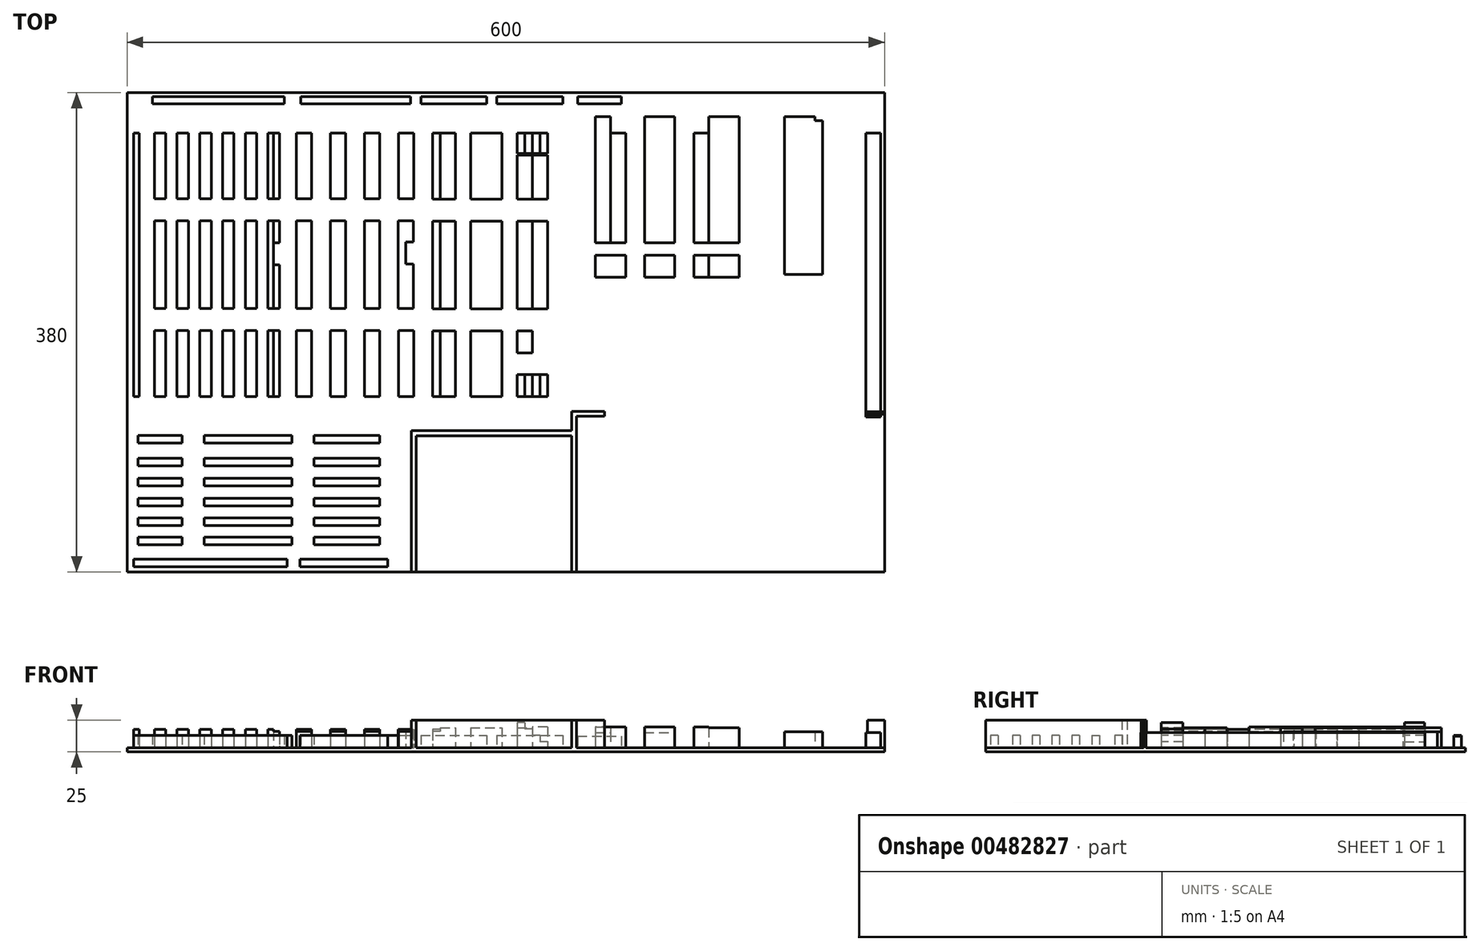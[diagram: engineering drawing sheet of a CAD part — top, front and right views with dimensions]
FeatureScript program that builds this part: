
annotation { "Feature Type Name" : "Feature", "Feature Type Description" : "" }
export const myFeature = defineFeature(function(context is Context, id is Id, definition is map)
    precondition{}
    {
        {
            var Q0;
            Q0=qCreatedBy(makeId("Top.planeOp"),FACE);
            var sketch = newSketch(context, id + "F0", { "sketchPlane" : qUnion([Q0])});
            skLineSegment(sketch, "E0.bottom", {"start": v(300, 190) * mm, "end": v(-300, 190) * mm});
            skLineSegment(sketch, "E0.top", {"start": v(300, -190) * mm, "end": v(-300, -190) * mm});
            skLineSegment(sketch, "E0.left", {"start": v(300, 190) * mm, "end": v(300, -190) * mm});
            skLineSegment(sketch, "E0.right", {"start": v(-300, 190) * mm, "end": v(-300, -190) * mm});
            skPoint(sketch, "E0.middle", {"position": v(0, 0) * mm});
            skLineSegment(sketch, "E1", {"start": v(-75, -78) * mm, "end": v(-75, -190) * mm});
            skLineSegment(sketch, "E2", {"start": v(-75, -78) * mm, "end": v(52, -78) * mm});
            skLineSegment(sketch, "E3", {"start": v(300, -63) * mm, "end": v(286.5, -63) * mm});
            skLineSegment(sketch, "E4", {"start": v(52, -78) * mm, "end": v(52, -62.65) * mm});
            skLineSegment(sketch, "E5", {"start": v(52, -62.65) * mm, "end": v(78, -62.65) * mm});
            skLineSegment(sketch, "E6.0", {"start": v(56, -66.65) * mm, "end": v(78, -66.65) * mm});
            skLineSegment(sketch, "E6.1", {"start": v(56, -78) * mm, "end": v(56, -66.65) * mm});
            skLineSegment(sketch, "E6.2", {"start": v(56, -78) * mm, "end": v(56, -190) * mm});
            skLineSegment(sketch, "E7", {"start": v(78, -62.65) * mm, "end": v(78, -66.65) * mm});
            skLineSegment(sketch, "E8.0", {"start": v(300, -65) * mm, "end": v(286.5, -65) * mm});
            skLineSegment(sketch, "E9", {"start": v(286.5, -63) * mm, "end": v(286.5, -65) * mm});
            skLineSegment(sketch, "E10.0", {"start": v(-71, -82) * mm, "end": v(-71, -190) * mm});
            skLineSegment(sketch, "E10.1", {"start": v(-71, -82) * mm, "end": v(52, -82) * mm});
            skLineSegment(sketch, "E11.0", {"start": v(52, -82) * mm, "end": v(52, -190) * mm});
            skLineSegment(sketch, "E12.0", {"start": v(304, 194) * mm, "end": v(-304, 194) * mm});
            skLineSegment(sketch, "E12.1", {"start": v(304, 194) * mm, "end": v(304, -194) * mm});
            skLineSegment(sketch, "E12.2", {"start": v(304, -194) * mm, "end": v(-304, -194) * mm});
            skLineSegment(sketch, "E12.3", {"start": v(-304, 194) * mm, "end": v(-304, -194) * mm});
            skLineSegment(sketch, "E13.bottom", {"start": v(-280, 187) * mm, "end": v(-175.6, 187) * mm});
            skLineSegment(sketch, "E13.top", {"start": v(-280, 181) * mm, "end": v(-175.6, 181) * mm});
            skLineSegment(sketch, "E13.left", {"start": v(-280, 187) * mm, "end": v(-280, 181) * mm});
            skLineSegment(sketch, "E13.right", {"start": v(-175.6, 187) * mm, "end": v(-175.6, 181) * mm});
            skLineSegment(sketch, "E14.bottom", {"start": v(-162.42, 187) * mm, "end": v(-75.42, 187) * mm});
            skLineSegment(sketch, "E14.top", {"start": v(-162.42, 181) * mm, "end": v(-75.42, 181) * mm});
            skLineSegment(sketch, "E14.left", {"start": v(-162.42, 187) * mm, "end": v(-162.42, 181) * mm});
            skLineSegment(sketch, "E14.right", {"start": v(-75.42, 187) * mm, "end": v(-75.42, 181) * mm});
            skLineSegment(sketch, "E15.bottom", {"start": v(-67.42, 187) * mm, "end": v(-15.22, 187) * mm});
            skLineSegment(sketch, "E15.top", {"start": v(-67.42, 181) * mm, "end": v(-15.22, 181) * mm});
            skLineSegment(sketch, "E15.left", {"start": v(-67.42, 187) * mm, "end": v(-67.42, 181) * mm});
            skLineSegment(sketch, "E15.right", {"start": v(-15.22, 187) * mm, "end": v(-15.22, 181) * mm});
            skLineSegment(sketch, "E16.bottom", {"start": v(56.8, 187) * mm, "end": v(91.6, 187) * mm});
            skLineSegment(sketch, "E16.top", {"start": v(56.8, 181) * mm, "end": v(91.6, 181) * mm});
            skLineSegment(sketch, "E16.left", {"start": v(56.8, 187) * mm, "end": v(56.8, 181) * mm});
            skLineSegment(sketch, "E16.right", {"start": v(91.6, 187) * mm, "end": v(91.6, 181) * mm});
            skLineSegment(sketch, "E17.bottom", {"start": v(-295, 158) * mm, "end": v(-290.5, 158) * mm});
            skLineSegment(sketch, "E17.top", {"start": v(-295, 18.8) * mm, "end": v(-290.5, 18.8) * mm});
            skLineSegment(sketch, "E17.left", {"start": v(-295, 158) * mm, "end": v(-295, 18.8) * mm});
            skLineSegment(sketch, "E17.right", {"start": v(-290.5, 158) * mm, "end": v(-290.5, 18.8) * mm});
            skLineSegment(sketch, "E18.top", {"start": v(-295, -50.8) * mm, "end": v(-290.5, -50.8) * mm});
            skLineSegment(sketch, "E18.left", {"start": v(-295, 18.8) * mm, "end": v(-295, -50.8) * mm});
            skLineSegment(sketch, "E18.right", {"start": v(-290.5, 18.8) * mm, "end": v(-290.5, -50.8) * mm});
            skLineSegment(sketch, "E19.bottom", {"start": v(-278.5, 158) * mm, "end": v(-269.5, 158) * mm});
            skLineSegment(sketch, "E19.top", {"start": v(-278.5, 105.8) * mm, "end": v(-269.5, 105.8) * mm});
            skLineSegment(sketch, "E19.left", {"start": v(-278.5, 158) * mm, "end": v(-278.5, 105.8) * mm});
            skLineSegment(sketch, "E19.right", {"start": v(-269.5, 158) * mm, "end": v(-269.5, 105.8) * mm});
            skLineSegment(sketch, "E20.1.0.0", {"start": v(-260.5, 158) * mm, "end": v(-251.5, 158) * mm});
            skLineSegment(sketch, "E20.1.0.1", {"start": v(-260.5, 158) * mm, "end": v(-260.5, 105.8) * mm});
            skLineSegment(sketch, "E20.1.0.2", {"start": v(-251.5, 158) * mm, "end": v(-251.5, 105.8) * mm});
            skLineSegment(sketch, "E20.1.0.3", {"start": v(-260.5, 105.8) * mm, "end": v(-251.5, 105.8) * mm});
            skLineSegment(sketch, "E20.2.0.0", {"start": v(-242.5, 158) * mm, "end": v(-233.5, 158) * mm});
            skLineSegment(sketch, "E20.2.0.1", {"start": v(-242.5, 158) * mm, "end": v(-242.5, 105.8) * mm});
            skLineSegment(sketch, "E20.2.0.2", {"start": v(-233.5, 158) * mm, "end": v(-233.5, 105.8) * mm});
            skLineSegment(sketch, "E20.2.0.3", {"start": v(-242.5, 105.8) * mm, "end": v(-233.5, 105.8) * mm});
            skLineSegment(sketch, "E20.3.0.0", {"start": v(-224.5, 158) * mm, "end": v(-215.5, 158) * mm});
            skLineSegment(sketch, "E20.3.0.1", {"start": v(-224.5, 158) * mm, "end": v(-224.5, 105.8) * mm});
            skLineSegment(sketch, "E20.3.0.2", {"start": v(-215.5, 158) * mm, "end": v(-215.5, 105.8) * mm});
            skLineSegment(sketch, "E20.3.0.3", {"start": v(-224.5, 105.8) * mm, "end": v(-215.5, 105.8) * mm});
            skLineSegment(sketch, "E20.4.0.0", {"start": v(-206.5, 158) * mm, "end": v(-197.5, 158) * mm});
            skLineSegment(sketch, "E20.4.0.1", {"start": v(-206.5, 158) * mm, "end": v(-206.5, 105.8) * mm});
            skLineSegment(sketch, "E20.4.0.2", {"start": v(-197.5, 158) * mm, "end": v(-197.5, 105.8) * mm});
            skLineSegment(sketch, "E20.4.0.3", {"start": v(-206.5, 105.8) * mm, "end": v(-197.5, 105.8) * mm});
            skLineSegment(sketch, "E21.bottom", {"start": v(-278.5, 88.4) * mm, "end": v(-269.5, 88.4) * mm});
            skLineSegment(sketch, "E21.top", {"start": v(-278.5, 18.8) * mm, "end": v(-269.5, 18.8) * mm});
            skLineSegment(sketch, "E21.left", {"start": v(-278.5, 88.4) * mm, "end": v(-278.5, 18.8) * mm});
            skLineSegment(sketch, "E21.right", {"start": v(-269.5, 88.4) * mm, "end": v(-269.5, 18.8) * mm});
            skLineSegment(sketch, "E22.1.0.0", {"start": v(-260.5, 88.4) * mm, "end": v(-251.5, 88.4) * mm});
            skLineSegment(sketch, "E22.1.0.1", {"start": v(-251.5, 88.4) * mm, "end": v(-251.5, 18.8) * mm});
            skLineSegment(sketch, "E22.1.0.2", {"start": v(-260.5, 88.4) * mm, "end": v(-260.5, 18.8) * mm});
            skLineSegment(sketch, "E22.1.0.3", {"start": v(-260.5, 18.8) * mm, "end": v(-251.5, 18.8) * mm});
            skLineSegment(sketch, "E22.2.0.0", {"start": v(-242.5, 88.4) * mm, "end": v(-233.5, 88.4) * mm});
            skLineSegment(sketch, "E22.2.0.1", {"start": v(-233.5, 88.4) * mm, "end": v(-233.5, 18.8) * mm});
            skLineSegment(sketch, "E22.2.0.2", {"start": v(-242.5, 88.4) * mm, "end": v(-242.5, 18.8) * mm});
            skLineSegment(sketch, "E22.2.0.3", {"start": v(-242.5, 18.8) * mm, "end": v(-233.5, 18.8) * mm});
            skLineSegment(sketch, "E22.3.0.0", {"start": v(-224.5, 88.4) * mm, "end": v(-215.5, 88.4) * mm});
            skLineSegment(sketch, "E22.3.0.1", {"start": v(-215.5, 88.4) * mm, "end": v(-215.5, 18.8) * mm});
            skLineSegment(sketch, "E22.3.0.2", {"start": v(-224.5, 88.4) * mm, "end": v(-224.5, 18.8) * mm});
            skLineSegment(sketch, "E22.3.0.3", {"start": v(-224.5, 18.8) * mm, "end": v(-215.5, 18.8) * mm});
            skLineSegment(sketch, "E22.4.0.0", {"start": v(-206.5, 88.4) * mm, "end": v(-197.5, 88.4) * mm});
            skLineSegment(sketch, "E22.4.0.1", {"start": v(-197.5, 88.4) * mm, "end": v(-197.5, 18.8) * mm});
            skLineSegment(sketch, "E22.4.0.2", {"start": v(-206.5, 88.4) * mm, "end": v(-206.5, 18.8) * mm});
            skLineSegment(sketch, "E22.4.0.3", {"start": v(-206.5, 18.8) * mm, "end": v(-197.5, 18.8) * mm});
            skLineSegment(sketch, "E23.bottom", {"start": v(-278.5, 1.4) * mm, "end": v(-269.5, 1.4) * mm});
            skLineSegment(sketch, "E23.top", {"start": v(-278.5, -50.8) * mm, "end": v(-269.5, -50.8) * mm});
            skLineSegment(sketch, "E23.left", {"start": v(-278.5, 1.4) * mm, "end": v(-278.5, -50.8) * mm});
            skLineSegment(sketch, "E23.right", {"start": v(-269.5, 1.4) * mm, "end": v(-269.5, -50.8) * mm});
            skLineSegment(sketch, "E24.1.0.0", {"start": v(-260.5, 1.4) * mm, "end": v(-260.5, -50.8) * mm});
            skLineSegment(sketch, "E24.1.0.1", {"start": v(-260.5, 1.4) * mm, "end": v(-251.5, 1.4) * mm});
            skLineSegment(sketch, "E24.1.0.2", {"start": v(-251.5, 1.4) * mm, "end": v(-251.5, -50.8) * mm});
            skLineSegment(sketch, "E24.1.0.3", {"start": v(-260.5, -50.8) * mm, "end": v(-251.5, -50.8) * mm});
            skLineSegment(sketch, "E24.2.0.0", {"start": v(-242.5, 1.4) * mm, "end": v(-242.5, -50.8) * mm});
            skLineSegment(sketch, "E24.2.0.1", {"start": v(-242.5, 1.4) * mm, "end": v(-233.5, 1.4) * mm});
            skLineSegment(sketch, "E24.2.0.2", {"start": v(-233.5, 1.4) * mm, "end": v(-233.5, -50.8) * mm});
            skLineSegment(sketch, "E24.2.0.3", {"start": v(-242.5, -50.8) * mm, "end": v(-233.5, -50.8) * mm});
            skLineSegment(sketch, "E24.3.0.0", {"start": v(-224.5, 1.4) * mm, "end": v(-224.5, -50.8) * mm});
            skLineSegment(sketch, "E24.3.0.1", {"start": v(-224.5, 1.4) * mm, "end": v(-215.5, 1.4) * mm});
            skLineSegment(sketch, "E24.3.0.2", {"start": v(-215.5, 1.4) * mm, "end": v(-215.5, -50.8) * mm});
            skLineSegment(sketch, "E24.3.0.3", {"start": v(-224.5, -50.8) * mm, "end": v(-215.5, -50.8) * mm});
            skLineSegment(sketch, "E24.4.0.0", {"start": v(-206.5, 1.4) * mm, "end": v(-206.5, -50.8) * mm});
            skLineSegment(sketch, "E24.4.0.1", {"start": v(-206.5, 1.4) * mm, "end": v(-197.5, 1.4) * mm});
            skLineSegment(sketch, "E24.4.0.2", {"start": v(-197.5, 1.4) * mm, "end": v(-197.5, -50.8) * mm});
            skLineSegment(sketch, "E24.4.0.3", {"start": v(-206.5, -50.8) * mm, "end": v(-197.5, -50.8) * mm});
            skLineSegment(sketch, "E25.bottom", {"start": v(-188.5, 1.4) * mm, "end": v(-184, 1.4) * mm});
            skLineSegment(sketch, "E25.top", {"start": v(-188.5, -50.8) * mm, "end": v(-184, -50.8) * mm});
            skLineSegment(sketch, "E25.left", {"start": v(-188.5, 1.4) * mm, "end": v(-188.5, -50.8) * mm});
            skLineSegment(sketch, "E25.right", {"start": v(-184, 1.4) * mm, "end": v(-184, -50.8) * mm});
            skLineSegment(sketch, "E26.bottom", {"start": v(-188.5, 158) * mm, "end": v(-184, 158) * mm});
            skLineSegment(sketch, "E26.top", {"start": v(-188.5, 105.8) * mm, "end": v(-184, 105.8) * mm});
            skLineSegment(sketch, "E26.left", {"start": v(-188.5, 158) * mm, "end": v(-188.5, 105.8) * mm});
            skLineSegment(sketch, "E26.right", {"start": v(-184, 158) * mm, "end": v(-184, 105.8) * mm});
            skLineSegment(sketch, "E27.bottom", {"start": v(-188.5, 88.4) * mm, "end": v(-184, 88.4) * mm});
            skLineSegment(sketch, "E27.top", {"start": v(-188.5, 18.8) * mm, "end": v(-184, 18.8) * mm});
            skLineSegment(sketch, "E27.left", {"start": v(-188.5, 88.4) * mm, "end": v(-188.5, 18.8) * mm});
            skLineSegment(sketch, "E27.right", {"start": v(-184, 88.4) * mm, "end": v(-184, 18.8) * mm});
            skLineSegment(sketch, "E28", {"start": v(-184, 1.4) * mm, "end": v(-179.5, 1.4) * mm});
            skLineSegment(sketch, "E29", {"start": v(-179.5, 1.4) * mm, "end": v(-179.5, -50.8) * mm});
            skLineSegment(sketch, "E30", {"start": v(-179.5, -50.8) * mm, "end": v(-184, -50.8) * mm});
            skLineSegment(sketch, "E31", {"start": v(-184, 88.4) * mm, "end": v(-179.5, 88.4) * mm});
            skLineSegment(sketch, "E32", {"start": v(-179.5, 18.8) * mm, "end": v(-184, 18.8) * mm});
            skLineSegment(sketch, "E33", {"start": v(-184, 158) * mm, "end": v(-179.5, 158) * mm});
            skLineSegment(sketch, "E34", {"start": v(-179.5, 158) * mm, "end": v(-179.5, 105.8) * mm});
            skLineSegment(sketch, "E35", {"start": v(-179.5, 105.8) * mm, "end": v(-184, 105.8) * mm});
            skLineSegment(sketch, "E36", {"start": v(-179.5, 88.4) * mm, "end": v(-179.5, 71) * mm});
            skLineSegment(sketch, "E37", {"start": v(-179.5, 71) * mm, "end": v(-184, 71) * mm});
            skLineSegment(sketch, "E38", {"start": v(-179.5, 18.8) * mm, "end": v(-179.5, 53.6) * mm});
            skLineSegment(sketch, "E39", {"start": v(-179.5, 53.6) * mm, "end": v(-184, 53.6) * mm});
            skLineSegment(sketch, "E40.bottom", {"start": v(-166, 158) * mm, "end": v(-154, 158) * mm});
            skLineSegment(sketch, "E40.top", {"start": v(-166, 105.8) * mm, "end": v(-154, 105.8) * mm});
            skLineSegment(sketch, "E40.left", {"start": v(-166, 158) * mm, "end": v(-166, 105.8) * mm});
            skLineSegment(sketch, "E40.right", {"start": v(-154, 158) * mm, "end": v(-154, 105.8) * mm});
            skLineSegment(sketch, "E41.bottom", {"start": v(-166, 88.4) * mm, "end": v(-154, 88.4) * mm});
            skLineSegment(sketch, "E41.top", {"start": v(-166, 18.8) * mm, "end": v(-154, 18.8) * mm});
            skLineSegment(sketch, "E41.left", {"start": v(-166, 88.4) * mm, "end": v(-166, 18.8) * mm});
            skLineSegment(sketch, "E41.right", {"start": v(-154, 88.4) * mm, "end": v(-154, 18.8) * mm});
            skLineSegment(sketch, "E42.bottom", {"start": v(-166, 1.4) * mm, "end": v(-154, 1.4) * mm});
            skLineSegment(sketch, "E42.top", {"start": v(-166, -50.8) * mm, "end": v(-154, -50.8) * mm});
            skLineSegment(sketch, "E42.left", {"start": v(-166, 1.4) * mm, "end": v(-166, -50.8) * mm});
            skLineSegment(sketch, "E42.right", {"start": v(-154, 1.4) * mm, "end": v(-154, -50.8) * mm});
            skLineSegment(sketch, "E43.1.0.0", {"start": v(-139, 158) * mm, "end": v(-127, 158) * mm});
            skLineSegment(sketch, "E43.1.0.1", {"start": v(-139, 158) * mm, "end": v(-139, 105.8) * mm});
            skLineSegment(sketch, "E43.1.0.2", {"start": v(-127, 158) * mm, "end": v(-127, 105.8) * mm});
            skLineSegment(sketch, "E43.1.0.3", {"start": v(-139, 105.8) * mm, "end": v(-127, 105.8) * mm});
            skLineSegment(sketch, "E43.1.0.4", {"start": v(-139, 88.4) * mm, "end": v(-127, 88.4) * mm});
            skLineSegment(sketch, "E43.1.0.5", {"start": v(-139, 88.4) * mm, "end": v(-139, 18.8) * mm});
            skLineSegment(sketch, "E43.1.0.6", {"start": v(-127, 88.4) * mm, "end": v(-127, 18.8) * mm});
            skLineSegment(sketch, "E43.1.0.7", {"start": v(-139, 18.8) * mm, "end": v(-127, 18.8) * mm});
            skLineSegment(sketch, "E43.1.0.8", {"start": v(-139, 1.4) * mm, "end": v(-127, 1.4) * mm});
            skLineSegment(sketch, "E43.1.0.9", {"start": v(-127, 1.4) * mm, "end": v(-127, -50.8) * mm});
            skLineSegment(sketch, "E43.1.0.10", {"start": v(-139, 1.4) * mm, "end": v(-139, -50.8) * mm});
            skLineSegment(sketch, "E43.1.0.11", {"start": v(-139, -50.8) * mm, "end": v(-127, -50.8) * mm});
            skLineSegment(sketch, "E43.2.0.0", {"start": v(-112, 158) * mm, "end": v(-100, 158) * mm});
            skLineSegment(sketch, "E43.2.0.1", {"start": v(-112, 158) * mm, "end": v(-112, 105.8) * mm});
            skLineSegment(sketch, "E43.2.0.2", {"start": v(-100, 158) * mm, "end": v(-100, 105.8) * mm});
            skLineSegment(sketch, "E43.2.0.3", {"start": v(-112, 105.8) * mm, "end": v(-100, 105.8) * mm});
            skLineSegment(sketch, "E43.2.0.4", {"start": v(-112, 88.4) * mm, "end": v(-100, 88.4) * mm});
            skLineSegment(sketch, "E43.2.0.5", {"start": v(-112, 88.4) * mm, "end": v(-112, 18.8) * mm});
            skLineSegment(sketch, "E43.2.0.6", {"start": v(-100, 88.4) * mm, "end": v(-100, 18.8) * mm});
            skLineSegment(sketch, "E43.2.0.7", {"start": v(-112, 18.8) * mm, "end": v(-100, 18.8) * mm});
            skLineSegment(sketch, "E43.2.0.8", {"start": v(-112, 1.4) * mm, "end": v(-100, 1.4) * mm});
            skLineSegment(sketch, "E43.2.0.9", {"start": v(-100, 1.4) * mm, "end": v(-100, -50.8) * mm});
            skLineSegment(sketch, "E43.2.0.10", {"start": v(-112, 1.4) * mm, "end": v(-112, -50.8) * mm});
            skLineSegment(sketch, "E43.2.0.11", {"start": v(-112, -50.8) * mm, "end": v(-100, -50.8) * mm});
            skLineSegment(sketch, "E43.3.0.0", {"start": v(-85, 158) * mm, "end": v(-73, 158) * mm});
            skLineSegment(sketch, "E43.3.0.1", {"start": v(-85, 158) * mm, "end": v(-85, 105.8) * mm});
            skLineSegment(sketch, "E43.3.0.2", {"start": v(-73, 158) * mm, "end": v(-73, 105.8) * mm});
            skLineSegment(sketch, "E43.3.0.3", {"start": v(-85, 105.8) * mm, "end": v(-73, 105.8) * mm});
            skLineSegment(sketch, "E43.3.0.4", {"start": v(-85.36, 88.4) * mm, "end": v(-73.36, 88.4) * mm});
            skLineSegment(sketch, "E43.3.0.5", {"start": v(-85.36, 88.4) * mm, "end": v(-85.36, 18.8) * mm});
            skLineSegment(sketch, "E43.3.0.7", {"start": v(-85.36, 18.8) * mm, "end": v(-73.36, 18.8) * mm});
            skLineSegment(sketch, "E43.3.0.8", {"start": v(-85, 1.4) * mm, "end": v(-73, 1.4) * mm});
            skLineSegment(sketch, "E43.3.0.9", {"start": v(-73, 1.4) * mm, "end": v(-73, -50.8) * mm});
            skLineSegment(sketch, "E43.3.0.10", {"start": v(-85, 1.4) * mm, "end": v(-85, -50.8) * mm});
            skLineSegment(sketch, "E43.3.0.11", {"start": v(-85, -50.8) * mm, "end": v(-73, -50.8) * mm});
            skLineSegment(sketch, "E44.bottom", {"start": v(-52, 157.8) * mm, "end": v(-40, 157.8) * mm});
            skLineSegment(sketch, "E44.top", {"start": v(-52, 105.6) * mm, "end": v(-40, 105.6) * mm});
            skLineSegment(sketch, "E44.left", {"start": v(-52, 157.8) * mm, "end": v(-52, 105.6) * mm});
            skLineSegment(sketch, "E44.right", {"start": v(-40, 157.8) * mm, "end": v(-40, 105.6) * mm});
            skLineSegment(sketch, "E45.bottom", {"start": v(-52, 88.2) * mm, "end": v(-40, 88.2) * mm});
            skLineSegment(sketch, "E45.top", {"start": v(-52, 18.6) * mm, "end": v(-40, 18.6) * mm});
            skLineSegment(sketch, "E45.left", {"start": v(-52, 88.2) * mm, "end": v(-52, 18.6) * mm});
            skLineSegment(sketch, "E45.right", {"start": v(-40, 88.2) * mm, "end": v(-40, 18.6) * mm});
            skLineSegment(sketch, "E46.bottom", {"start": v(-52, 1.2) * mm, "end": v(-40, 1.2) * mm});
            skLineSegment(sketch, "E46.top", {"start": v(-52, -51) * mm, "end": v(-40, -51) * mm});
            skLineSegment(sketch, "E46.left", {"start": v(-52, 1.2) * mm, "end": v(-52, -51) * mm});
            skLineSegment(sketch, "E46.right", {"start": v(-40, 1.2) * mm, "end": v(-40, -51) * mm});
            skLineSegment(sketch, "E47", {"start": v(-52, 157.8) * mm, "end": v(-58, 157.8) * mm});
            skLineSegment(sketch, "E48", {"start": v(-58, 157.8) * mm, "end": v(-58, 105.6) * mm});
            skLineSegment(sketch, "E49", {"start": v(-58, 105.6) * mm, "end": v(-52, 105.6) * mm});
            skLineSegment(sketch, "E50", {"start": v(-52, 88.2) * mm, "end": v(-58, 88.2) * mm});
            skLineSegment(sketch, "E51", {"start": v(-58, 88.2) * mm, "end": v(-58, 18.6) * mm});
            skLineSegment(sketch, "E52", {"start": v(-58, 18.6) * mm, "end": v(-52, 18.6) * mm});
            skLineSegment(sketch, "E53", {"start": v(-52, 1.2) * mm, "end": v(-58, 1.2) * mm});
            skLineSegment(sketch, "E54", {"start": v(-58, 1.2) * mm, "end": v(-58, -51) * mm});
            skLineSegment(sketch, "E55", {"start": v(-58, -51) * mm, "end": v(-52, -51) * mm});
            skLineSegment(sketch, "E56.bottom", {"start": v(-7.22, 187) * mm, "end": v(44.98, 187) * mm});
            skLineSegment(sketch, "E56.top", {"start": v(-7.22, 181) * mm, "end": v(44.98, 181) * mm});
            skLineSegment(sketch, "E56.left", {"start": v(-7.22, 187) * mm, "end": v(-7.22, 181) * mm});
            skLineSegment(sketch, "E56.right", {"start": v(44.98, 187) * mm, "end": v(44.98, 181) * mm});
            skLineSegment(sketch, "E57.bottom", {"start": v(-28, 157.8) * mm, "end": v(-3, 157.8) * mm});
            skLineSegment(sketch, "E58.bottom", {"start": v(-28, 88.2) * mm, "end": v(-3, 88.2) * mm});
            skLineSegment(sketch, "E58.top", {"start": v(-28, 18.6) * mm, "end": v(-3, 18.6) * mm});
            skLineSegment(sketch, "E58.left", {"start": v(-28, 88.2) * mm, "end": v(-28, 18.6) * mm});
            skLineSegment(sketch, "E58.right", {"start": v(-3, 88.2) * mm, "end": v(-3, 18.6) * mm});
            skLineSegment(sketch, "E59.bottom", {"start": v(-28, 1.2) * mm, "end": v(-3, 1.2) * mm});
            skLineSegment(sketch, "E59.top", {"start": v(-28, -51) * mm, "end": v(-3, -51) * mm});
            skLineSegment(sketch, "E59.left", {"start": v(-28, 1.2) * mm, "end": v(-28, -51) * mm});
            skLineSegment(sketch, "E59.right", {"start": v(-3, 1.2) * mm, "end": v(-3, -51) * mm});
            skLineSegment(sketch, "E60", {"start": v(-73.36, 88.4) * mm, "end": v(-73.36, 71.67) * mm});
            skLineSegment(sketch, "E61", {"start": v(-73.36, 71.67) * mm, "end": v(-79.36, 71.67) * mm});
            skLineSegment(sketch, "E62", {"start": v(-79.36, 71.67) * mm, "end": v(-79.36, 54.27) * mm});
            skLineSegment(sketch, "E63", {"start": v(-79.36, 54.27) * mm, "end": v(-73.36, 54.27) * mm});
            skLineSegment(sketch, "E64", {"start": v(-73.36, 54.27) * mm, "end": v(-73.36, 18.8) * mm});
            skLineSegment(sketch, "E65.top", {"start": v(9, 140.6) * mm, "end": v(21, 140.6) * mm});
            skLineSegment(sketch, "E66.top", {"start": v(9, 18.6) * mm, "end": v(21, 18.6) * mm});
            skLineSegment(sketch, "E66.left", {"start": v(9, 88.2) * mm, "end": v(9, 18.6) * mm});
            skLineSegment(sketch, "E66.right", {"start": v(21, 88.2) * mm, "end": v(21, 18.6) * mm});
            skLineSegment(sketch, "E67.bottom", {"start": v(9, 1.2) * mm, "end": v(21, 1.2) * mm});
            skLineSegment(sketch, "E67.top", {"start": v(9, -16.2) * mm, "end": v(21, -16.2) * mm});
            skLineSegment(sketch, "E67.left", {"start": v(9, 1.2) * mm, "end": v(9, -16.2) * mm});
            skLineSegment(sketch, "E67.right", {"start": v(21, 1.2) * mm, "end": v(21, -16.2) * mm});
            skLineSegment(sketch, "E68", {"start": v(21, 157.8) * mm, "end": v(21, 141.8) * mm});
            skLineSegment(sketch, "E69", {"start": v(33, 140.6) * mm, "end": v(21, 140.6) * mm});
            skLineSegment(sketch, "E70", {"start": v(9, 141.8) * mm, "end": v(9, 157.8) * mm});
            skLineSegment(sketch, "E71", {"start": v(9, 157.8) * mm, "end": v(33, 157.8) * mm});
            skLineSegment(sketch, "E72", {"start": v(33, 157.8) * mm, "end": v(33, 141.8) * mm});
            skLineSegment(sketch, "E73", {"start": v(27, 141.8) * mm, "end": v(27, 157.8) * mm});
            skLineSegment(sketch, "E74", {"start": v(15, 141.8) * mm, "end": v(15, 157.8) * mm});
            skLineSegment(sketch, "E75", {"start": v(9, -51) * mm, "end": v(21, -51) * mm});
            skLineSegment(sketch, "E76", {"start": v(33, -51) * mm, "end": v(33, -33.6) * mm});
            skLineSegment(sketch, "E77", {"start": v(33, -33.6) * mm, "end": v(21, -33.6) * mm});
            skLineSegment(sketch, "E78", {"start": v(9, -33.6) * mm, "end": v(9, -51) * mm});
            skLineSegment(sketch, "E79", {"start": v(21, -33.6) * mm, "end": v(21, -51) * mm});
            skLineSegment(sketch, "E80", {"start": v(21, -33.6) * mm, "end": v(9, -33.6) * mm});
            skLineSegment(sketch, "E81", {"start": v(21, -51) * mm, "end": v(33, -51) * mm});
            skLineSegment(sketch, "E82", {"start": v(27, -33.6) * mm, "end": v(27, -51) * mm});
            skLineSegment(sketch, "E83", {"start": v(15, -51) * mm, "end": v(15, -33.6) * mm});
            skLineSegment(sketch, "E84.bottom", {"start": v(70.8, 171) * mm, "end": v(82.8, 171) * mm});
            skLineSegment(sketch, "E84.top", {"start": v(70.8, 71) * mm, "end": v(82.8, 71) * mm});
            skLineSegment(sketch, "E84.left", {"start": v(70.8, 171) * mm, "end": v(70.8, 71) * mm});
            skLineSegment(sketch, "E84.right", {"start": v(82.8, 171) * mm, "end": v(82.8, 71) * mm});
            skLineSegment(sketch, "E85", {"start": v(82.8, 71) * mm, "end": v(94.8, 71) * mm});
            skLineSegment(sketch, "E86", {"start": v(94.8, 71) * mm, "end": v(94.8, 158) * mm});
            skLineSegment(sketch, "E87", {"start": v(94.8, 158) * mm, "end": v(82.8, 158) * mm});
            skLineSegment(sketch, "E88", {"start": v(109.8, 171) * mm, "end": v(133.8, 171) * mm});
            skLineSegment(sketch, "E89", {"start": v(133.8, 171) * mm, "end": v(133.8, 71) * mm});
            skLineSegment(sketch, "E90", {"start": v(133.8, 71) * mm, "end": v(109.8, 71) * mm});
            skLineSegment(sketch, "E91", {"start": v(109.8, 71) * mm, "end": v(109.8, 171) * mm});
            skLineSegment(sketch, "E92", {"start": v(148.8, 158) * mm, "end": v(160.8, 158) * mm});
            skLineSegment(sketch, "E93", {"start": v(148.8, 71) * mm, "end": v(160.8, 71) * mm});
            skLineSegment(sketch, "E94", {"start": v(160.8, 71) * mm, "end": v(160.8, 158) * mm});
            skLineSegment(sketch, "E95", {"start": v(148.8, 158) * mm, "end": v(148.8, 71) * mm});
            skLineSegment(sketch, "E96", {"start": v(160.8, 71) * mm, "end": v(184.8, 71) * mm});
            skLineSegment(sketch, "E97", {"start": v(184.8, 71) * mm, "end": v(184.8, 171) * mm});
            skLineSegment(sketch, "E98", {"start": v(184.8, 171) * mm, "end": v(160.8, 171) * mm});
            skLineSegment(sketch, "E99", {"start": v(160.8, 171) * mm, "end": v(160.8, 158) * mm});
            skLineSegment(sketch, "E100.bottom", {"start": v(220.8, 171) * mm, "end": v(244.8, 171) * mm});
            skLineSegment(sketch, "E100.top", {"start": v(220.8, 46) * mm, "end": v(244.8, 46) * mm});
            skLineSegment(sketch, "E100.left", {"start": v(220.8, 171) * mm, "end": v(220.8, 46) * mm});
            skLineSegment(sketch, "E100.right", {"start": v(244.8, 171) * mm, "end": v(244.8, 46) * mm});
            skLineSegment(sketch, "E101", {"start": v(244.8, 46) * mm, "end": v(250.8, 46) * mm});
            skLineSegment(sketch, "E102", {"start": v(250.8, 46) * mm, "end": v(250.8, 167.8) * mm});
            skLineSegment(sketch, "E103", {"start": v(250.8, 167.8) * mm, "end": v(244.8, 167.8) * mm});
            skLineSegment(sketch, "E104", {"start": v(285, 158) * mm, "end": v(297, 158) * mm});
            skLineSegment(sketch, "E105", {"start": v(297, 158) * mm, "end": v(297, 83) * mm});
            skLineSegment(sketch, "E106", {"start": v(297, 83) * mm, "end": v(285, 83) * mm});
            skLineSegment(sketch, "E107", {"start": v(285, 83) * mm, "end": v(285, 158) * mm});
            skLineSegment(sketch, "E108", {"start": v(285, 83) * mm, "end": v(285, -67) * mm});
            skLineSegment(sketch, "E109", {"start": v(285, -67) * mm, "end": v(297, -67) * mm});
            skLineSegment(sketch, "E110", {"start": v(297, -67) * mm, "end": v(297, 158) * mm});
            skLineSegment(sketch, "E111", {"start": v(-28, 157.8) * mm, "end": v(-28, 105.6) * mm});
            skLineSegment(sketch, "E112", {"start": v(-28, 105.6) * mm, "end": v(-3, 105.6) * mm});
            skLineSegment(sketch, "E113", {"start": v(-3, 105.6) * mm, "end": v(-3, 157.8) * mm});
            skLineSegment(sketch, "E114", {"start": v(9, 140.6) * mm, "end": v(9, 105.6) * mm});
            skLineSegment(sketch, "E115", {"start": v(9, 105.6) * mm, "end": v(21, 105.6) * mm});
            skLineSegment(sketch, "E116", {"start": v(21, 105.6) * mm, "end": v(21, 140.6) * mm});
            skLineSegment(sketch, "E117", {"start": v(33, 140.6) * mm, "end": v(33, 105.6) * mm});
            skLineSegment(sketch, "E118", {"start": v(33, 105.6) * mm, "end": v(21, 105.6) * mm});
            skLineSegment(sketch, "E119", {"start": v(9, 88.2) * mm, "end": v(21, 88.2) * mm});
            skLineSegment(sketch, "E120", {"start": v(33, 88.2) * mm, "end": v(21, 88.2) * mm});
            skLineSegment(sketch, "E121", {"start": v(33, 88.2) * mm, "end": v(33, 18.6) * mm});
            skLineSegment(sketch, "E122", {"start": v(33, 18.6) * mm, "end": v(21, 18.6) * mm});
            skLineSegment(sketch, "E123", {"start": v(33, 157.8) * mm, "end": v(43.65, 157.8) * mm, "construction": true});
            skLineSegment(sketch, "E124", {"start": v(43.65, 157.8) * mm, "end": v(43.65, 141.8) * mm, "construction": true});
            skLineSegment(sketch, "E125", {"start": v(33, 141.8) * mm, "end": v(9, 141.8) * mm});
            skLineSegment(sketch, "E126", {"start": v(70.8, 61) * mm, "end": v(70.8, 43.6) * mm});
            skLineSegment(sketch, "E127", {"start": v(70.8, 43.6) * mm, "end": v(94.8, 43.6) * mm});
            skLineSegment(sketch, "E128", {"start": v(94.8, 43.6) * mm, "end": v(94.8, 61) * mm});
            skLineSegment(sketch, "E129", {"start": v(94.8, 61) * mm, "end": v(70.8, 61) * mm});
            skLineSegment(sketch, "E130.bottom", {"start": v(109.8, 61) * mm, "end": v(133.8, 61) * mm});
            skLineSegment(sketch, "E130.top", {"start": v(109.8, 43.6) * mm, "end": v(133.8, 43.6) * mm});
            skLineSegment(sketch, "E130.left", {"start": v(109.8, 61) * mm, "end": v(109.8, 43.6) * mm});
            skLineSegment(sketch, "E130.right", {"start": v(133.8, 61) * mm, "end": v(133.8, 43.6) * mm});
            skLineSegment(sketch, "E131.bottom", {"start": v(148.8, 61) * mm, "end": v(184.8, 61) * mm});
            skLineSegment(sketch, "E131.top", {"start": v(148.8, 43.6) * mm, "end": v(184.8, 43.6) * mm});
            skLineSegment(sketch, "E131.left", {"start": v(148.8, 61) * mm, "end": v(148.8, 43.6) * mm});
            skLineSegment(sketch, "E131.right", {"start": v(184.8, 61) * mm, "end": v(184.8, 43.6) * mm});
            skLineSegment(sketch, "E132", {"start": v(160.8, 61) * mm, "end": v(160.8, 43.6) * mm});
            skLineSegment(sketch, "E133", {"start": v(-100, -81.8) * mm, "end": v(-152.2, -81.8) * mm});
            skLineSegment(sketch, "E134", {"start": v(-169.6, -81.8) * mm, "end": v(-239.2, -81.8) * mm});
            skLineSegment(sketch, "E135", {"start": v(-256.6, -81.8) * mm, "end": v(-291.4, -81.8) * mm});
            skLineSegment(sketch, "E136", {"start": v(-100, -81.8) * mm, "end": v(-100, -87.8) * mm});
            skLineSegment(sketch, "E137", {"start": v(-100, -87.8) * mm, "end": v(-152.2, -87.8) * mm});
            skLineSegment(sketch, "E138", {"start": v(-152.2, -87.8) * mm, "end": v(-152.2, -81.8) * mm});
            skLineSegment(sketch, "E139", {"start": v(-169.6, -81.8) * mm, "end": v(-169.6, -87.8) * mm});
            skLineSegment(sketch, "E140", {"start": v(-169.6, -87.8) * mm, "end": v(-239.2, -87.8) * mm});
            skLineSegment(sketch, "E141", {"start": v(-239.2, -81.8) * mm, "end": v(-239.2, -87.8) * mm});
            skLineSegment(sketch, "E142", {"start": v(-256.6, -81.8) * mm, "end": v(-256.6, -87.8) * mm});
            skLineSegment(sketch, "E143", {"start": v(-256.6, -87.8) * mm, "end": v(-291.4, -87.8) * mm});
            skLineSegment(sketch, "E144", {"start": v(-291.4, -87.8) * mm, "end": v(-291.4, -81.8) * mm});
            skLineSegment(sketch, "E145", {"start": v(-291.4, -99.8) * mm, "end": v(-256.6, -99.8) * mm});
            skLineSegment(sketch, "E146", {"start": v(-256.6, -99.8) * mm, "end": v(-256.6, -105.8) * mm});
            skLineSegment(sketch, "E147", {"start": v(-256.6, -105.8) * mm, "end": v(-291.4, -105.8) * mm});
            skLineSegment(sketch, "E148", {"start": v(-291.4, -105.8) * mm, "end": v(-291.4, -99.8) * mm});
            skLineSegment(sketch, "E149", {"start": v(-239.2, -99.8) * mm, "end": v(-169.6, -99.8) * mm});
            skLineSegment(sketch, "E150", {"start": v(-169.6, -99.8) * mm, "end": v(-169.6, -105.8) * mm});
            skLineSegment(sketch, "E151", {"start": v(-169.6, -105.8) * mm, "end": v(-239.2, -105.8) * mm});
            skLineSegment(sketch, "E152", {"start": v(-239.2, -105.8) * mm, "end": v(-239.2, -99.8) * mm});
            skLineSegment(sketch, "E153", {"start": v(-152.2, -99.8) * mm, "end": v(-100, -99.8) * mm});
            skLineSegment(sketch, "E154", {"start": v(-100, -99.8) * mm, "end": v(-100, -105.8) * mm});
            skLineSegment(sketch, "E155", {"start": v(-100, -105.8) * mm, "end": v(-152.2, -105.8) * mm});
            skLineSegment(sketch, "E156", {"start": v(-152.2, -105.8) * mm, "end": v(-152.2, -99.8) * mm});
            skLineSegment(sketch, "E157", {"start": v(-239.2, -115.7) * mm, "end": v(-169.6, -115.7) * mm});
            skLineSegment(sketch, "E158", {"start": v(-169.6, -115.7) * mm, "end": v(-169.6, -121.7) * mm});
            skLineSegment(sketch, "E159", {"start": v(-169.6, -131.5) * mm, "end": v(-169.6, -137.5) * mm});
            skLineSegment(sketch, "E160", {"start": v(-169.6, -147.12) * mm, "end": v(-169.6, -153.12) * mm});
            skLineSegment(sketch, "E161", {"start": v(-169.6, -162.5) * mm, "end": v(-169.6, -168.5) * mm});
            skLineSegment(sketch, "E162", {"start": v(-169.6, -168.5) * mm, "end": v(-239.2, -168.5) * mm});
            skLineSegment(sketch, "E163", {"start": v(-239.2, -168.5) * mm, "end": v(-239.2, -162.5) * mm});
            skLineSegment(sketch, "E164", {"start": v(-239.2, -162.5) * mm, "end": v(-169.6, -162.5) * mm});
            skLineSegment(sketch, "E165", {"start": v(-169.6, -153.12) * mm, "end": v(-239.2, -153.12) * mm});
            skLineSegment(sketch, "E166", {"start": v(-169.6, -147.12) * mm, "end": v(-239.2, -147.12) * mm});
            skLineSegment(sketch, "E167", {"start": v(-239.2, -147.12) * mm, "end": v(-239.2, -153.12) * mm});
            skLineSegment(sketch, "E168", {"start": v(-239.2, -115.7) * mm, "end": v(-239.2, -121.7) * mm});
            skLineSegment(sketch, "E169", {"start": v(-239.2, -121.7) * mm, "end": v(-169.6, -121.7) * mm});
            skLineSegment(sketch, "E170", {"start": v(-169.6, -131.5) * mm, "end": v(-239.2, -131.5) * mm});
            skLineSegment(sketch, "E171", {"start": v(-239.2, -131.5) * mm, "end": v(-239.2, -137.5) * mm});
            skLineSegment(sketch, "E172", {"start": v(-169.6, -137.5) * mm, "end": v(-239.2, -137.5) * mm});
            skLineSegment(sketch, "E173.bottom", {"start": v(-256.6, -115.7) * mm, "end": v(-291.4, -115.7) * mm});
            skLineSegment(sketch, "E173.top", {"start": v(-256.6, -121.7) * mm, "end": v(-291.4, -121.7) * mm});
            skLineSegment(sketch, "E173.left", {"start": v(-256.6, -115.7) * mm, "end": v(-256.6, -121.7) * mm});
            skLineSegment(sketch, "E173.right", {"start": v(-291.4, -115.7) * mm, "end": v(-291.4, -121.7) * mm});
            skLineSegment(sketch, "E174.bottom", {"start": v(-256.6, -131.5) * mm, "end": v(-291.4, -131.5) * mm});
            skLineSegment(sketch, "E174.top", {"start": v(-256.6, -137.5) * mm, "end": v(-291.4, -137.5) * mm});
            skLineSegment(sketch, "E174.left", {"start": v(-256.6, -131.5) * mm, "end": v(-256.6, -137.5) * mm});
            skLineSegment(sketch, "E174.right", {"start": v(-291.4, -131.5) * mm, "end": v(-291.4, -137.5) * mm});
            skLineSegment(sketch, "E175.bottom", {"start": v(-256.6, -147.12) * mm, "end": v(-291.4, -147.12) * mm});
            skLineSegment(sketch, "E175.top", {"start": v(-256.6, -153.12) * mm, "end": v(-291.4, -153.12) * mm});
            skLineSegment(sketch, "E175.left", {"start": v(-256.6, -147.12) * mm, "end": v(-256.6, -153.12) * mm});
            skLineSegment(sketch, "E175.right", {"start": v(-291.4, -147.12) * mm, "end": v(-291.4, -153.12) * mm});
            skLineSegment(sketch, "E176.bottom", {"start": v(-256.6, -162.5) * mm, "end": v(-291.4, -162.5) * mm});
            skLineSegment(sketch, "E176.top", {"start": v(-256.6, -168.5) * mm, "end": v(-291.4, -168.5) * mm});
            skLineSegment(sketch, "E176.left", {"start": v(-256.6, -162.5) * mm, "end": v(-256.6, -168.5) * mm});
            skLineSegment(sketch, "E176.right", {"start": v(-291.4, -162.5) * mm, "end": v(-291.4, -168.5) * mm});
            skLineSegment(sketch, "E177.bottom", {"start": v(-152.2, -115.7) * mm, "end": v(-100, -115.7) * mm});
            skLineSegment(sketch, "E177.top", {"start": v(-152.2, -121.7) * mm, "end": v(-100, -121.7) * mm});
            skLineSegment(sketch, "E177.left", {"start": v(-152.2, -115.7) * mm, "end": v(-152.2, -121.7) * mm});
            skLineSegment(sketch, "E177.right", {"start": v(-100, -115.7) * mm, "end": v(-100, -121.7) * mm});
            skLineSegment(sketch, "E178.bottom", {"start": v(-100, -131.5) * mm, "end": v(-152.2, -131.5) * mm});
            skLineSegment(sketch, "E178.top", {"start": v(-100, -137.5) * mm, "end": v(-152.2, -137.5) * mm});
            skLineSegment(sketch, "E178.left", {"start": v(-100, -131.5) * mm, "end": v(-100, -137.5) * mm});
            skLineSegment(sketch, "E178.right", {"start": v(-152.2, -131.5) * mm, "end": v(-152.2, -137.5) * mm});
            skLineSegment(sketch, "E179.bottom", {"start": v(-152.2, -147.12) * mm, "end": v(-100, -147.12) * mm});
            skLineSegment(sketch, "E179.top", {"start": v(-152.2, -153.12) * mm, "end": v(-100, -153.12) * mm});
            skLineSegment(sketch, "E179.left", {"start": v(-152.2, -147.12) * mm, "end": v(-152.2, -153.12) * mm});
            skLineSegment(sketch, "E179.right", {"start": v(-100, -147.12) * mm, "end": v(-100, -153.12) * mm});
            skLineSegment(sketch, "E180.bottom", {"start": v(-100, -162.5) * mm, "end": v(-152.2, -162.5) * mm});
            skLineSegment(sketch, "E180.top", {"start": v(-100, -168.5) * mm, "end": v(-152.2, -168.5) * mm});
            skLineSegment(sketch, "E180.left", {"start": v(-100, -162.5) * mm, "end": v(-100, -168.5) * mm});
            skLineSegment(sketch, "E180.right", {"start": v(-152.2, -162.5) * mm, "end": v(-152.2, -168.5) * mm});
            skLineSegment(sketch, "E181.bottom", {"start": v(-93.6, -180) * mm, "end": v(-163.2, -180) * mm});
            skLineSegment(sketch, "E181.top", {"start": v(-93.6, -186) * mm, "end": v(-163.2, -186) * mm});
            skLineSegment(sketch, "E181.left", {"start": v(-93.6, -180) * mm, "end": v(-93.6, -186) * mm});
            skLineSegment(sketch, "E181.right", {"start": v(-163.2, -180) * mm, "end": v(-163.2, -186) * mm});
            skLineSegment(sketch, "E182.bottom", {"start": v(-173.2, -180) * mm, "end": v(-295, -180) * mm});
            skLineSegment(sketch, "E182.top", {"start": v(-173.2, -186) * mm, "end": v(-295, -186) * mm});
            skLineSegment(sketch, "E182.left", {"start": v(-173.2, -180) * mm, "end": v(-173.2, -186) * mm});
            skLineSegment(sketch, "E182.right", {"start": v(-295, -180) * mm, "end": v(-295, -186) * mm});
            skSolve(sketch);
        }
        {
            var Q0;
            {var subQ7=sQuery(id+"F0.wireOp",EDGE,"E0.bottom");Q0=makeQuery(id+"F0.imprint","IMPRINT",FACE,{"disambiguationData":[TD([[makeQuery(id+"F0.imprint","IMPRINT",EDGE,{"derivedFrom":subQ7}),1.0]])]});}
            extrude(context, id + "F1", {"entities" : qUnion([Q0]), "depth" : 3 * mm, "offsetDistance" : 25 * mm});
        }
        {
            var Q0;
            {var subQ0=sQuery(id+"F0.wireOp",EDGE,"E1");Q0=makeQuery(id+"F0.imprint","IMPRINT",FACE,{"disambiguationData":[TD([[makeQuery(id+"F0.imprint","IMPRINT",EDGE,{"derivedFrom":subQ0}),1.0]])]});}
            var Q1;
            {var subQ0=sQuery(id+"F0.wireOp",EDGE,"E3");Q1=makeQuery(id+"F0.imprint","IMPRINT",FACE,{"disambiguationData":[TD([[makeQuery(id+"F0.imprint","IMPRINT",EDGE,{"derivedFrom":subQ0}),1.0]])]});}
            extrude(context, id + "F2", {"entities" : qUnion([Q0, Q1]), "operationType" : NewBodyOperationType.ADD, "depth" : 25 * mm, "offsetDistance" : 25 * mm});
        }
        {
            var Q0;
            {var subQ0=sQuery(id+"F0.wireOp",EDGE,"E10.0");Q0=makeQuery(id+"F0.imprint","IMPRINT",FACE,{"disambiguationData":[TD([[makeQuery(id+"F0.imprint","IMPRINT",EDGE,{"derivedFrom":subQ0}),1.0]])]});}
            extrude(context, id + "F3", {"entities" : qUnion([Q0]), "operationType" : NewBodyOperationType.ADD, "depth" : 3 * mm});
        }
        {
            var Q0;
            {var subQ0=sQuery(id+"F0.wireOp",EDGE,"E70");Q0=makeQuery(id+"F0.imprint","IMPRINT",FACE,{"disambiguationData":[TD([[makeQuery(id+"F0.imprint","IMPRINT",EDGE,{"derivedFrom":subQ0}),-1.0]])]});}
            var Q1;
            {var subQ0=sQuery(id+"F0.wireOp",EDGE,"E78");Q1=makeQuery(id+"F0.imprint","IMPRINT",FACE,{"disambiguationData":[TD([[makeQuery(id+"F0.imprint","IMPRINT",EDGE,{"derivedFrom":subQ0}),1.0]])]});}
            extrude(context, id + "F4", {"entities" : qUnion([Q0, Q1]), "operationType" : NewBodyOperationType.ADD, "depth" : 23 * mm, "offsetDistance" : 25 * mm});
        }
        {
            var Q0;
            {var subQ0=sQuery(id+"F0.wireOp",EDGE,"E68");Q0=makeQuery(id+"F0.imprint","IMPRINT",FACE,{"disambiguationData":[TD([[makeQuery(id+"F0.imprint","IMPRINT",EDGE,{"derivedFrom":subQ0}),-1.0]])]});}
            var Q1;
            {var subQ0=sQuery(id+"F0.wireOp",EDGE,"E79");Q1=makeQuery(id+"F0.imprint","IMPRINT",FACE,{"disambiguationData":[TD([[makeQuery(id+"F0.imprint","IMPRINT",EDGE,{"derivedFrom":subQ0}),-1.0]])]});}
            extrude(context, id + "F5", {"entities" : qUnion([Q0, Q1]), "operationType" : NewBodyOperationType.ADD, "depth" : 18 * mm, "offsetDistance" : 25 * mm});
        }
        {
            var Q0;
            {var subQ0=sQuery(id+"F0.wireOp",EDGE,"E68");Q0=makeQuery(id+"F0.imprint","IMPRINT",FACE,{"disambiguationData":[TD([[makeQuery(id+"F0.imprint","IMPRINT",EDGE,{"derivedFrom":subQ0}),1.0]])]});}
            var Q1;
            {var subQ0=sQuery(id+"F0.wireOp",EDGE,"E79");Q1=makeQuery(id+"F0.imprint","IMPRINT",FACE,{"disambiguationData":[TD([[makeQuery(id+"F0.imprint","IMPRINT",EDGE,{"derivedFrom":subQ0}),1.0]])]});}
            extrude(context, id + "F6", {"entities" : qUnion([Q0, Q1]), "operationType" : NewBodyOperationType.ADD, "depth" : 13 * mm, "offsetDistance" : 25 * mm});
        }
        {
            var Q0;
            {var subQ0=sQuery(id+"F0.wireOp",EDGE,"E72");Q0=makeQuery(id+"F0.imprint","IMPRINT",FACE,{"disambiguationData":[TD([[makeQuery(id+"F0.imprint","IMPRINT",EDGE,{"derivedFrom":subQ0}),-1.0]])]});}
            var Q1;
            {var subQ0=sQuery(id+"F0.wireOp",EDGE,"E76");Q1=makeQuery(id+"F0.imprint","IMPRINT",FACE,{"disambiguationData":[TD([[makeQuery(id+"F0.imprint","IMPRINT",EDGE,{"derivedFrom":subQ0}),1.0]])]});}
            extrude(context, id + "F7", {"entities" : qUnion([Q0, Q1]), "operationType" : NewBodyOperationType.ADD, "depth" : 8 * mm, "offsetDistance" : 25 * mm});
        }
        {
            var Q0;
            Q0=makeQuery(id+"F0.imprint","IMPRINT",FACE,{"disambiguationData":[TD([[makeQuery(id+"F0.imprint","IMPRINT",EDGE,{"derivedFrom":sQuery(id+"F0.wireOp",EDGE,"E25.right")}),1.0]])]});
            var Q1;
            Q1=makeQuery(id+"F0.imprint","IMPRINT",FACE,{"disambiguationData":[TD([[makeQuery(id+"F0.imprint","IMPRINT",EDGE,{"derivedFrom":sQuery(id+"F0.wireOp",EDGE,"E42.bottom")}),-1.0]])]});
            var Q2;
            Q2=makeQuery(id+"F0.imprint","IMPRINT",FACE,{"disambiguationData":[TD([[makeQuery(id+"F0.imprint","IMPRINT",EDGE,{"derivedFrom":sQuery(id+"F0.wireOp",EDGE,"E43.1.0.8")}),-1.0]])]});
            var Q3;
            Q3=makeQuery(id+"F0.imprint","IMPRINT",FACE,{"disambiguationData":[TD([[makeQuery(id+"F0.imprint","IMPRINT",EDGE,{"derivedFrom":sQuery(id+"F0.wireOp",EDGE,"E43.2.0.8")}),-1.0]])]});
            var Q4;
            Q4=makeQuery(id+"F0.imprint","IMPRINT",FACE,{"disambiguationData":[TD([[makeQuery(id+"F0.imprint","IMPRINT",EDGE,{"derivedFrom":sQuery(id+"F0.wireOp",EDGE,"E43.3.0.8")}),-1.0]])]});
            var Q5;
            Q5=makeQuery(id+"F0.imprint","IMPRINT",FACE,{"disambiguationData":[TD([[makeQuery(id+"F0.imprint","IMPRINT",EDGE,{"derivedFrom":sQuery(id+"F0.wireOp",EDGE,"E46.left")}),-1.0]])]});
            var Q6;
            {var subQ0=sQuery(id+"F0.wireOp",EDGE,"E31");Q6=makeQuery(id+"F0.imprint","IMPRINT",FACE,{"disambiguationData":[TD([[makeQuery(id+"F0.imprint","IMPRINT",EDGE,{"derivedFrom":subQ0}),-1.0]])]});}
            var Q7;
            {var subQ0=sQuery(id+"F0.wireOp",EDGE,"E32");Q7=makeQuery(id+"F0.imprint","IMPRINT",FACE,{"disambiguationData":[TD([[makeQuery(id+"F0.imprint","IMPRINT",EDGE,{"derivedFrom":subQ0}),-1.0]])]});}
            var Q8;
            Q8=makeQuery(id+"F0.imprint","IMPRINT",FACE,{"disambiguationData":[TD([[makeQuery(id+"F0.imprint","IMPRINT",EDGE,{"derivedFrom":sQuery(id+"F0.wireOp",EDGE,"E26.right")}),1.0]])]});
            extrude(context, id + "F8", {"entities" : qUnion([Q0, Q1, Q2, Q3, Q4, Q5, Q6, Q7, Q8]), "operationType" : NewBodyOperationType.ADD, "depth" : 16.2 * mm, "offsetDistance" : 25 * mm});
        }
        {
            var Q0;
            Q0=makeQuery(id+"F0.imprint","IMPRINT",FACE,{"disambiguationData":[TD([[makeQuery(id+"F0.imprint","IMPRINT",EDGE,{"derivedFrom":sQuery(id+"F0.wireOp",EDGE,"E17.top")}),-1.0]])]});
            var Q1;
            Q1=makeQuery(id+"F0.imprint","IMPRINT",FACE,{"disambiguationData":[TD([[makeQuery(id+"F0.imprint","IMPRINT",EDGE,{"derivedFrom":sQuery(id+"F0.wireOp",EDGE,"E23.bottom")}),-1.0]])]});
            var Q2;
            Q2=makeQuery(id+"F0.imprint","IMPRINT",FACE,{"disambiguationData":[TD([[makeQuery(id+"F0.imprint","IMPRINT",EDGE,{"derivedFrom":sQuery(id+"F0.wireOp",EDGE,"E24.1.0.0")}),1.0]])]});
            var Q3;
            Q3=makeQuery(id+"F0.imprint","IMPRINT",FACE,{"disambiguationData":[TD([[makeQuery(id+"F0.imprint","IMPRINT",EDGE,{"derivedFrom":sQuery(id+"F0.wireOp",EDGE,"E24.2.0.0")}),1.0]])]});
            var Q4;
            Q4=makeQuery(id+"F0.imprint","IMPRINT",FACE,{"disambiguationData":[TD([[makeQuery(id+"F0.imprint","IMPRINT",EDGE,{"derivedFrom":sQuery(id+"F0.wireOp",EDGE,"E24.3.0.0")}),1.0]])]});
            var Q5;
            Q5=makeQuery(id+"F0.imprint","IMPRINT",FACE,{"disambiguationData":[TD([[makeQuery(id+"F0.imprint","IMPRINT",EDGE,{"derivedFrom":sQuery(id+"F0.wireOp",EDGE,"E24.4.0.0")}),1.0]])]});
            var Q6;
            Q6=makeQuery(id+"F0.imprint","IMPRINT",FACE,{"disambiguationData":[TD([[makeQuery(id+"F0.imprint","IMPRINT",EDGE,{"derivedFrom":sQuery(id+"F0.wireOp",EDGE,"E25.bottom")}),-1.0]])]});
            var Q7;
            Q7=makeQuery(id+"F0.imprint","IMPRINT",FACE,{"disambiguationData":[TD([[makeQuery(id+"F0.imprint","IMPRINT",EDGE,{"derivedFrom":sQuery(id+"F0.wireOp",EDGE,"E17.bottom")}),-1.0]])]});
            var Q8;
            Q8=makeQuery(id+"F0.imprint","IMPRINT",FACE,{"disambiguationData":[TD([[makeQuery(id+"F0.imprint","IMPRINT",EDGE,{"derivedFrom":sQuery(id+"F0.wireOp",EDGE,"E21.bottom")}),-1.0]])]});
            var Q9;
            Q9=makeQuery(id+"F0.imprint","IMPRINT",FACE,{"disambiguationData":[TD([[makeQuery(id+"F0.imprint","IMPRINT",EDGE,{"derivedFrom":sQuery(id+"F0.wireOp",EDGE,"E22.1.0.0")}),-1.0]])]});
            var Q10;
            Q10=makeQuery(id+"F0.imprint","IMPRINT",FACE,{"disambiguationData":[TD([[makeQuery(id+"F0.imprint","IMPRINT",EDGE,{"derivedFrom":sQuery(id+"F0.wireOp",EDGE,"E22.2.0.0")}),-1.0]])]});
            var Q11;
            Q11=makeQuery(id+"F0.imprint","IMPRINT",FACE,{"disambiguationData":[TD([[makeQuery(id+"F0.imprint","IMPRINT",EDGE,{"derivedFrom":sQuery(id+"F0.wireOp",EDGE,"E22.3.0.0")}),-1.0]])]});
            var Q12;
            Q12=makeQuery(id+"F0.imprint","IMPRINT",FACE,{"disambiguationData":[TD([[makeQuery(id+"F0.imprint","IMPRINT",EDGE,{"derivedFrom":sQuery(id+"F0.wireOp",EDGE,"E22.4.0.0")}),-1.0]])]});
            var Q13;
            {var subQ1=sQuery(id+"F0.wireOp",EDGE,"E27.bottom");Q13=makeQuery(id+"F0.imprint","IMPRINT",FACE,{"disambiguationData":[TD([[makeQuery(id+"F0.imprint","IMPRINT",EDGE,{"derivedFrom":subQ1}),-1.0]])]});}
            var Q14;
            Q14=makeQuery(id+"F0.imprint","IMPRINT",FACE,{"disambiguationData":[TD([[makeQuery(id+"F0.imprint","IMPRINT",EDGE,{"derivedFrom":sQuery(id+"F0.wireOp",EDGE,"E26.bottom")}),-1.0]])]});
            var Q15;
            Q15=makeQuery(id+"F0.imprint","IMPRINT",FACE,{"disambiguationData":[TD([[makeQuery(id+"F0.imprint","IMPRINT",EDGE,{"derivedFrom":sQuery(id+"F0.wireOp",EDGE,"E20.4.0.0")}),-1.0]])]});
            var Q16;
            Q16=makeQuery(id+"F0.imprint","IMPRINT",FACE,{"disambiguationData":[TD([[makeQuery(id+"F0.imprint","IMPRINT",EDGE,{"derivedFrom":sQuery(id+"F0.wireOp",EDGE,"E20.3.0.0")}),-1.0]])]});
            var Q17;
            Q17=makeQuery(id+"F0.imprint","IMPRINT",FACE,{"disambiguationData":[TD([[makeQuery(id+"F0.imprint","IMPRINT",EDGE,{"derivedFrom":sQuery(id+"F0.wireOp",EDGE,"E20.2.0.0")}),-1.0]])]});
            var Q18;
            Q18=makeQuery(id+"F0.imprint","IMPRINT",FACE,{"disambiguationData":[TD([[makeQuery(id+"F0.imprint","IMPRINT",EDGE,{"derivedFrom":sQuery(id+"F0.wireOp",EDGE,"E20.1.0.0")}),-1.0]])]});
            var Q19;
            Q19=makeQuery(id+"F0.imprint","IMPRINT",FACE,{"disambiguationData":[TD([[makeQuery(id+"F0.imprint","IMPRINT",EDGE,{"derivedFrom":sQuery(id+"F0.wireOp",EDGE,"E19.bottom")}),-1.0]])]});
            var Q20;
            Q20=makeQuery(id+"F0.imprint","IMPRINT",FACE,{"disambiguationData":[TD([[makeQuery(id+"F0.imprint","IMPRINT",EDGE,{"derivedFrom":sQuery(id+"F0.wireOp",EDGE,"E40.bottom")}),-1.0]])]});
            var Q21;
            Q21=makeQuery(id+"F0.imprint","IMPRINT",FACE,{"disambiguationData":[TD([[makeQuery(id+"F0.imprint","IMPRINT",EDGE,{"derivedFrom":sQuery(id+"F0.wireOp",EDGE,"E43.1.0.0")}),-1.0]])]});
            var Q22;
            Q22=makeQuery(id+"F0.imprint","IMPRINT",FACE,{"disambiguationData":[TD([[makeQuery(id+"F0.imprint","IMPRINT",EDGE,{"derivedFrom":sQuery(id+"F0.wireOp",EDGE,"E43.2.0.0")}),-1.0]])]});
            var Q23;
            Q23=makeQuery(id+"F0.imprint","IMPRINT",FACE,{"disambiguationData":[TD([[makeQuery(id+"F0.imprint","IMPRINT",EDGE,{"derivedFrom":sQuery(id+"F0.wireOp",EDGE,"E43.3.0.0")}),-1.0]])]});
            var Q24;
            Q24=makeQuery(id+"F0.imprint","IMPRINT",FACE,{"disambiguationData":[TD([[makeQuery(id+"F0.imprint","IMPRINT",EDGE,{"derivedFrom":sQuery(id+"F0.wireOp",EDGE,"E43.3.0.4")}),-1.0]])]});
            var Q25;
            Q25=makeQuery(id+"F0.imprint","IMPRINT",FACE,{"disambiguationData":[TD([[makeQuery(id+"F0.imprint","IMPRINT",EDGE,{"derivedFrom":sQuery(id+"F0.wireOp",EDGE,"E43.2.0.4")}),-1.0]])]});
            var Q26;
            Q26=makeQuery(id+"F0.imprint","IMPRINT",FACE,{"disambiguationData":[TD([[makeQuery(id+"F0.imprint","IMPRINT",EDGE,{"derivedFrom":sQuery(id+"F0.wireOp",EDGE,"E43.1.0.4")}),-1.0]])]});
            var Q27;
            Q27=makeQuery(id+"F0.imprint","IMPRINT",FACE,{"disambiguationData":[TD([[makeQuery(id+"F0.imprint","IMPRINT",EDGE,{"derivedFrom":sQuery(id+"F0.wireOp",EDGE,"E41.bottom")}),-1.0]])]});
            var Q28;
            Q28=makeQuery(id+"F0.imprint","IMPRINT",FACE,{"disambiguationData":[TD([[makeQuery(id+"F0.imprint","IMPRINT",EDGE,{"derivedFrom":sQuery(id+"F0.wireOp",EDGE,"E44.left")}),-1.0]])]});
            var Q29;
            Q29=makeQuery(id+"F0.imprint","IMPRINT",FACE,{"disambiguationData":[TD([[makeQuery(id+"F0.imprint","IMPRINT",EDGE,{"derivedFrom":sQuery(id+"F0.wireOp",EDGE,"E45.left")}),-1.0]])]});
            extrude(context, id + "F9", {"entities" : qUnion([Q0, Q1, Q2, Q3, Q4, Q5, Q6, Q7, Q8, Q9, Q10, Q11, Q12, Q13, Q14, Q15, Q16, Q17, Q18, Q19, Q20, Q21, Q22, Q23, Q24, Q25, Q26, Q27, Q28, Q29]), "operationType" : NewBodyOperationType.ADD, "depth" : 17.7 * mm, "offsetDistance" : 25 * mm});
        }
        {
            var Q0;
            Q0=makeQuery(id+"F0.imprint","IMPRINT",FACE,{"disambiguationData":[TD([[makeQuery(id+"F0.imprint","IMPRINT",EDGE,{"derivedFrom":sQuery(id+"F0.wireOp",EDGE,"E13.bottom")}),-1.0]])]});
            var Q1;
            Q1=makeQuery(id+"F0.imprint","IMPRINT",FACE,{"disambiguationData":[TD([[makeQuery(id+"F0.imprint","IMPRINT",EDGE,{"derivedFrom":sQuery(id+"F0.wireOp",EDGE,"E14.bottom")}),-1.0]])]});
            var Q2;
            Q2=makeQuery(id+"F0.imprint","IMPRINT",FACE,{"disambiguationData":[TD([[makeQuery(id+"F0.imprint","IMPRINT",EDGE,{"derivedFrom":sQuery(id+"F0.wireOp",EDGE,"E15.bottom")}),-1.0]])]});
            var Q3;
            Q3=makeQuery(id+"F0.imprint","IMPRINT",FACE,{"disambiguationData":[TD([[makeQuery(id+"F0.imprint","IMPRINT",EDGE,{"derivedFrom":sQuery(id+"F0.wireOp",EDGE,"E56.bottom")}),-1.0]])]});
            extrude(context, id + "F10", {"entities" : qUnion([Q0, Q1, Q2, Q3]), "operationType" : NewBodyOperationType.ADD, "depth" : 13 * mm, "offsetDistance" : 25 * mm});
        }
        {
            var Q0;
            Q0=makeQuery(id+"F0.imprint","IMPRINT",FACE,{"disambiguationData":[TD([[makeQuery(id+"F0.imprint","IMPRINT",EDGE,{"derivedFrom":sQuery(id+"F0.wireOp",EDGE,"E44.bottom")}),-1.0]])]});
            var Q1;
            Q1=makeQuery(id+"F0.imprint","IMPRINT",FACE,{"disambiguationData":[TD([[makeQuery(id+"F0.imprint","IMPRINT",EDGE,{"derivedFrom":sQuery(id+"F0.wireOp",EDGE,"E57.bottom")}),-1.0]])]});
            var Q2;
            Q2=makeQuery(id+"F0.imprint","IMPRINT",FACE,{"disambiguationData":[TD([[makeQuery(id+"F0.imprint","IMPRINT",EDGE,{"derivedFrom":sQuery(id+"F0.wireOp",EDGE,"E58.bottom")}),-1.0]])]});
            var Q3;
            Q3=makeQuery(id+"F0.imprint","IMPRINT",FACE,{"disambiguationData":[TD([[makeQuery(id+"F0.imprint","IMPRINT",EDGE,{"derivedFrom":sQuery(id+"F0.wireOp",EDGE,"E45.bottom")}),-1.0]])]});
            var Q4;
            Q4=makeQuery(id+"F0.imprint","IMPRINT",FACE,{"disambiguationData":[TD([[makeQuery(id+"F0.imprint","IMPRINT",EDGE,{"derivedFrom":sQuery(id+"F0.wireOp",EDGE,"E59.bottom")}),-1.0]])]});
            var Q5;
            Q5=makeQuery(id+"F0.imprint","IMPRINT",FACE,{"disambiguationData":[TD([[makeQuery(id+"F0.imprint","IMPRINT",EDGE,{"derivedFrom":sQuery(id+"F0.wireOp",EDGE,"E46.bottom")}),-1.0]])]});
            var Q6;
            Q6=makeQuery(id+"F0.imprint","IMPRINT",FACE,{"disambiguationData":[TD([[makeQuery(id+"F0.imprint","IMPRINT",EDGE,{"derivedFrom":sQuery(id+"F0.wireOp",EDGE,"E67.bottom")}),-1.0]])]});
            var Q7;
            Q7=makeQuery(id+"F0.imprint","IMPRINT",FACE,{"disambiguationData":[TD([[makeQuery(id+"F0.imprint","IMPRINT",EDGE,{"derivedFrom":sQuery(id+"F0.wireOp",EDGE,"E66.top")}),1.0]])]});
            var Q8;
            Q8=makeQuery(id+"F0.imprint","IMPRINT",FACE,{"disambiguationData":[TD([[makeQuery(id+"F0.imprint","IMPRINT",EDGE,{"derivedFrom":sQuery(id+"F0.wireOp",EDGE,"E65.top")}),-1.0]])]});
            extrude(context, id + "F11", {"entities" : qUnion([Q0, Q1, Q2, Q3, Q4, Q5, Q6, Q7, Q8]), "operationType" : NewBodyOperationType.ADD, "depth" : 19.1 * mm, "offsetDistance" : 25 * mm});
        }
        {
            var Q0;
            Q0=makeQuery(id+"F0.imprint","IMPRINT",FACE,{"disambiguationData":[TD([[makeQuery(id+"F0.imprint","IMPRINT",EDGE,{"derivedFrom":sQuery(id+"F0.wireOp",EDGE,"E16.bottom")}),-1.0]])]});
            extrude(context, id + "F12", {"entities" : qUnion([Q0]), "operationType" : NewBodyOperationType.ADD, "depth" : 12.2 * mm, "offsetDistance" : 25 * mm});
        }
        {
            var Q0;
            Q0=makeQuery(id+"F0.imprint","IMPRINT",FACE,{"disambiguationData":[TD([[makeQuery(id+"F0.imprint","IMPRINT",EDGE,{"derivedFrom":sQuery(id+"F0.wireOp",EDGE,"E69")}),1.0]])]});
            var Q1;
            Q1=makeQuery(id+"F0.imprint","IMPRINT",FACE,{"disambiguationData":[TD([[makeQuery(id+"F0.imprint","IMPRINT",EDGE,{"derivedFrom":sQuery(id+"F0.wireOp",EDGE,"E66.right")}),1.0]])]});
            var Q2;
            {var subQ0=sQuery(id+"F0.wireOp",EDGE,"E85");Q2=makeQuery(id+"F0.imprint","IMPRINT",FACE,{"disambiguationData":[TD([[makeQuery(id+"F0.imprint","IMPRINT",EDGE,{"derivedFrom":subQ0}),1.0]])]});}
            var Q3;
            Q3=makeQuery(id+"F0.imprint","IMPRINT",FACE,{"disambiguationData":[TD([[makeQuery(id+"F0.imprint","IMPRINT",EDGE,{"derivedFrom":sQuery(id+"F0.wireOp",EDGE,"E92")}),-1.0]])]});
            var Q4;
            Q4=makeQuery(id+"F0.imprint","IMPRINT",FACE,{"disambiguationData":[TD([[makeQuery(id+"F0.imprint","IMPRINT",EDGE,{"derivedFrom":sQuery(id+"F0.wireOp",EDGE,"E126")}),1.0]])]});
            var Q5;
            Q5=makeQuery(id+"F0.imprint","IMPRINT",FACE,{"disambiguationData":[TD([[makeQuery(id+"F0.imprint","IMPRINT",EDGE,{"derivedFrom":sQuery(id+"F0.wireOp",EDGE,"E130.bottom")}),-1.0]])]});
            var Q6;
            {var subQ0=sQuery(id+"F0.wireOp",EDGE,"E131.left");Q6=makeQuery(id+"F0.imprint","IMPRINT",FACE,{"disambiguationData":[TD([[makeQuery(id+"F0.imprint","IMPRINT",EDGE,{"derivedFrom":subQ0}),1.0]])]});}
            extrude(context, id + "F13", {"entities" : qUnion([Q0, Q1, Q2, Q3, Q4, Q5, Q6]), "operationType" : NewBodyOperationType.ADD, "depth" : 19.6 * mm, "offsetDistance" : 25 * mm});
        }
        {
            var Q0;
            {var subQ1=sQuery(id+"F0.wireOp",EDGE,"E84.bottom");Q0=makeQuery(id+"F0.imprint","IMPRINT",FACE,{"disambiguationData":[TD([[makeQuery(id+"F0.imprint","IMPRINT",EDGE,{"derivedFrom":subQ1}),-1.0]])]});}
            var Q1;
            Q1=makeQuery(id+"F0.imprint","IMPRINT",FACE,{"disambiguationData":[TD([[makeQuery(id+"F0.imprint","IMPRINT",EDGE,{"derivedFrom":sQuery(id+"F0.wireOp",EDGE,"E88")}),-1.0]])]});
            var Q2;
            {var subQ0=sQuery(id+"F0.wireOp",EDGE,"E104");Q2=makeQuery(id+"F0.imprint","IMPRINT",FACE,{"disambiguationData":[TD([[makeQuery(id+"F0.imprint","IMPRINT",EDGE,{"derivedFrom":subQ0}),-1.0]])]});}
            var Q3;
            {var subQ1=sQuery(id+"F0.wireOp",EDGE,"E9");Q3=makeQuery(id+"F0.imprint","IMPRINT",FACE,{"disambiguationData":[TD([[makeQuery(id+"F0.imprint","IMPRINT",EDGE,{"derivedFrom":subQ1}),-1.0]])]});}
            extrude(context, id + "F14", {"entities" : qUnion([Q0, Q1, Q2, Q3]), "operationType" : NewBodyOperationType.ADD, "depth" : 15.2 * mm, "offsetDistance" : 25 * mm});
        }
        {
            var Q0;
            Q0=makeQuery(id+"F0.imprint","IMPRINT",FACE,{"disambiguationData":[TD([[makeQuery(id+"F0.imprint","IMPRINT",EDGE,{"derivedFrom":sQuery(id+"F0.wireOp",EDGE,"E94")}),-1.0]])]});
            extrude(context, id + "F15", {"entities" : qUnion([Q0]), "operationType" : NewBodyOperationType.ADD, "depth" : 19 * mm, "offsetDistance" : 25 * mm});
        }
        {
            var Q0;
            {var subQ0=sQuery(id+"F0.wireOp",EDGE,"E101");Q0=makeQuery(id+"F0.imprint","IMPRINT",FACE,{"disambiguationData":[TD([[makeQuery(id+"F0.imprint","IMPRINT",EDGE,{"derivedFrom":subQ0}),1.0]])]});}
            var Q1;
            {var subQ1=sQuery(id+"F0.wireOp",EDGE,"E100.bottom");Q1=makeQuery(id+"F0.imprint","IMPRINT",FACE,{"disambiguationData":[TD([[makeQuery(id+"F0.imprint","IMPRINT",EDGE,{"derivedFrom":subQ1}),-1.0]])]});}
            extrude(context, id + "F16", {"entities" : qUnion([Q0, Q1]), "operationType" : NewBodyOperationType.ADD, "depth" : 15.7 * mm, "offsetDistance" : 25 * mm});
        }
        {
            var Q0;
            {var subQ0=sQuery(id+"F0.wireOp",EDGE,"E131.right");Q0=makeQuery(id+"F0.imprint","IMPRINT",FACE,{"disambiguationData":[TD([[makeQuery(id+"F0.imprint","IMPRINT",EDGE,{"derivedFrom":subQ0}),-1.0]])]});}
            extrude(context, id + "F17", {"entities" : qUnion([Q0]), "operationType" : NewBodyOperationType.ADD, "depth" : 19 * mm, "offsetDistance" : 25 * mm});
        }
        {
            var Q0;
            Q0=makeQuery(id+"F0.imprint","IMPRINT",FACE,{"disambiguationData":[TD([[makeQuery(id+"F0.imprint","IMPRINT",EDGE,{"derivedFrom":sQuery(id+"F0.wireOp",EDGE,"E135")}),1.0]])]});
            var Q1;
            Q1=makeQuery(id+"F0.imprint","IMPRINT",FACE,{"disambiguationData":[TD([[makeQuery(id+"F0.imprint","IMPRINT",EDGE,{"derivedFrom":sQuery(id+"F0.wireOp",EDGE,"E134")}),1.0]])]});
            var Q2;
            Q2=makeQuery(id+"F0.imprint","IMPRINT",FACE,{"disambiguationData":[TD([[makeQuery(id+"F0.imprint","IMPRINT",EDGE,{"derivedFrom":sQuery(id+"F0.wireOp",EDGE,"E133")}),1.0]])]});
            var Q3;
            Q3=makeQuery(id+"F0.imprint","IMPRINT",FACE,{"disambiguationData":[TD([[makeQuery(id+"F0.imprint","IMPRINT",EDGE,{"derivedFrom":sQuery(id+"F0.wireOp",EDGE,"E153")}),-1.0]])]});
            var Q4;
            Q4=makeQuery(id+"F0.imprint","IMPRINT",FACE,{"disambiguationData":[TD([[makeQuery(id+"F0.imprint","IMPRINT",EDGE,{"derivedFrom":sQuery(id+"F0.wireOp",EDGE,"E149")}),-1.0]])]});
            var Q5;
            Q5=makeQuery(id+"F0.imprint","IMPRINT",FACE,{"disambiguationData":[TD([[makeQuery(id+"F0.imprint","IMPRINT",EDGE,{"derivedFrom":sQuery(id+"F0.wireOp",EDGE,"E145")}),-1.0]])]});
            var Q6;
            Q6=makeQuery(id+"F0.imprint","IMPRINT",FACE,{"disambiguationData":[TD([[makeQuery(id+"F0.imprint","IMPRINT",EDGE,{"derivedFrom":sQuery(id+"F0.wireOp",EDGE,"E173.bottom")}),1.0]])]});
            var Q7;
            Q7=makeQuery(id+"F0.imprint","IMPRINT",FACE,{"disambiguationData":[TD([[makeQuery(id+"F0.imprint","IMPRINT",EDGE,{"derivedFrom":sQuery(id+"F0.wireOp",EDGE,"E157")}),-1.0]])]});
            var Q8;
            Q8=makeQuery(id+"F0.imprint","IMPRINT",FACE,{"disambiguationData":[TD([[makeQuery(id+"F0.imprint","IMPRINT",EDGE,{"derivedFrom":sQuery(id+"F0.wireOp",EDGE,"E177.bottom")}),-1.0]])]});
            var Q9;
            Q9=makeQuery(id+"F0.imprint","IMPRINT",FACE,{"disambiguationData":[TD([[makeQuery(id+"F0.imprint","IMPRINT",EDGE,{"derivedFrom":sQuery(id+"F0.wireOp",EDGE,"E178.bottom")}),1.0]])]});
            var Q10;
            Q10=makeQuery(id+"F0.imprint","IMPRINT",FACE,{"disambiguationData":[TD([[makeQuery(id+"F0.imprint","IMPRINT",EDGE,{"derivedFrom":sQuery(id+"F0.wireOp",EDGE,"E174.bottom")}),1.0]])]});
            var Q11;
            Q11=makeQuery(id+"F0.imprint","IMPRINT",FACE,{"disambiguationData":[TD([[makeQuery(id+"F0.imprint","IMPRINT",EDGE,{"derivedFrom":sQuery(id+"F0.wireOp",EDGE,"E159")}),-1.0]])]});
            var Q12;
            Q12=makeQuery(id+"F0.imprint","IMPRINT",FACE,{"disambiguationData":[TD([[makeQuery(id+"F0.imprint","IMPRINT",EDGE,{"derivedFrom":sQuery(id+"F0.wireOp",EDGE,"E175.bottom")}),1.0]])]});
            var Q13;
            Q13=makeQuery(id+"F0.imprint","IMPRINT",FACE,{"disambiguationData":[TD([[makeQuery(id+"F0.imprint","IMPRINT",EDGE,{"derivedFrom":sQuery(id+"F0.wireOp",EDGE,"E160")}),-1.0]])]});
            var Q14;
            Q14=makeQuery(id+"F0.imprint","IMPRINT",FACE,{"disambiguationData":[TD([[makeQuery(id+"F0.imprint","IMPRINT",EDGE,{"derivedFrom":sQuery(id+"F0.wireOp",EDGE,"E179.bottom")}),-1.0]])]});
            var Q15;
            Q15=makeQuery(id+"F0.imprint","IMPRINT",FACE,{"disambiguationData":[TD([[makeQuery(id+"F0.imprint","IMPRINT",EDGE,{"derivedFrom":sQuery(id+"F0.wireOp",EDGE,"E180.bottom")}),1.0]])]});
            var Q16;
            Q16=makeQuery(id+"F0.imprint","IMPRINT",FACE,{"disambiguationData":[TD([[makeQuery(id+"F0.imprint","IMPRINT",EDGE,{"derivedFrom":sQuery(id+"F0.wireOp",EDGE,"E161")}),-1.0]])]});
            var Q17;
            Q17=makeQuery(id+"F0.imprint","IMPRINT",FACE,{"disambiguationData":[TD([[makeQuery(id+"F0.imprint","IMPRINT",EDGE,{"derivedFrom":sQuery(id+"F0.wireOp",EDGE,"E176.bottom")}),1.0]])]});
            var Q18;
            Q18=makeQuery(id+"F0.imprint","IMPRINT",FACE,{"disambiguationData":[TD([[makeQuery(id+"F0.imprint","IMPRINT",EDGE,{"derivedFrom":sQuery(id+"F0.wireOp",EDGE,"E182.bottom")}),1.0]])]});
            var Q19;
            Q19=makeQuery(id+"F0.imprint","IMPRINT",FACE,{"disambiguationData":[TD([[makeQuery(id+"F0.imprint","IMPRINT",EDGE,{"derivedFrom":sQuery(id+"F0.wireOp",EDGE,"E181.bottom")}),1.0]])]});
            extrude(context, id + "F18", {"entities" : qUnion([Q0, Q1, Q2, Q3, Q4, Q5, Q6, Q7, Q8, Q9, Q10, Q11, Q12, Q13, Q14, Q15, Q16, Q17, Q18, Q19]), "operationType" : NewBodyOperationType.ADD, "depth" : 13 * mm, "offsetDistance" : 25 * mm});
        }
    });
